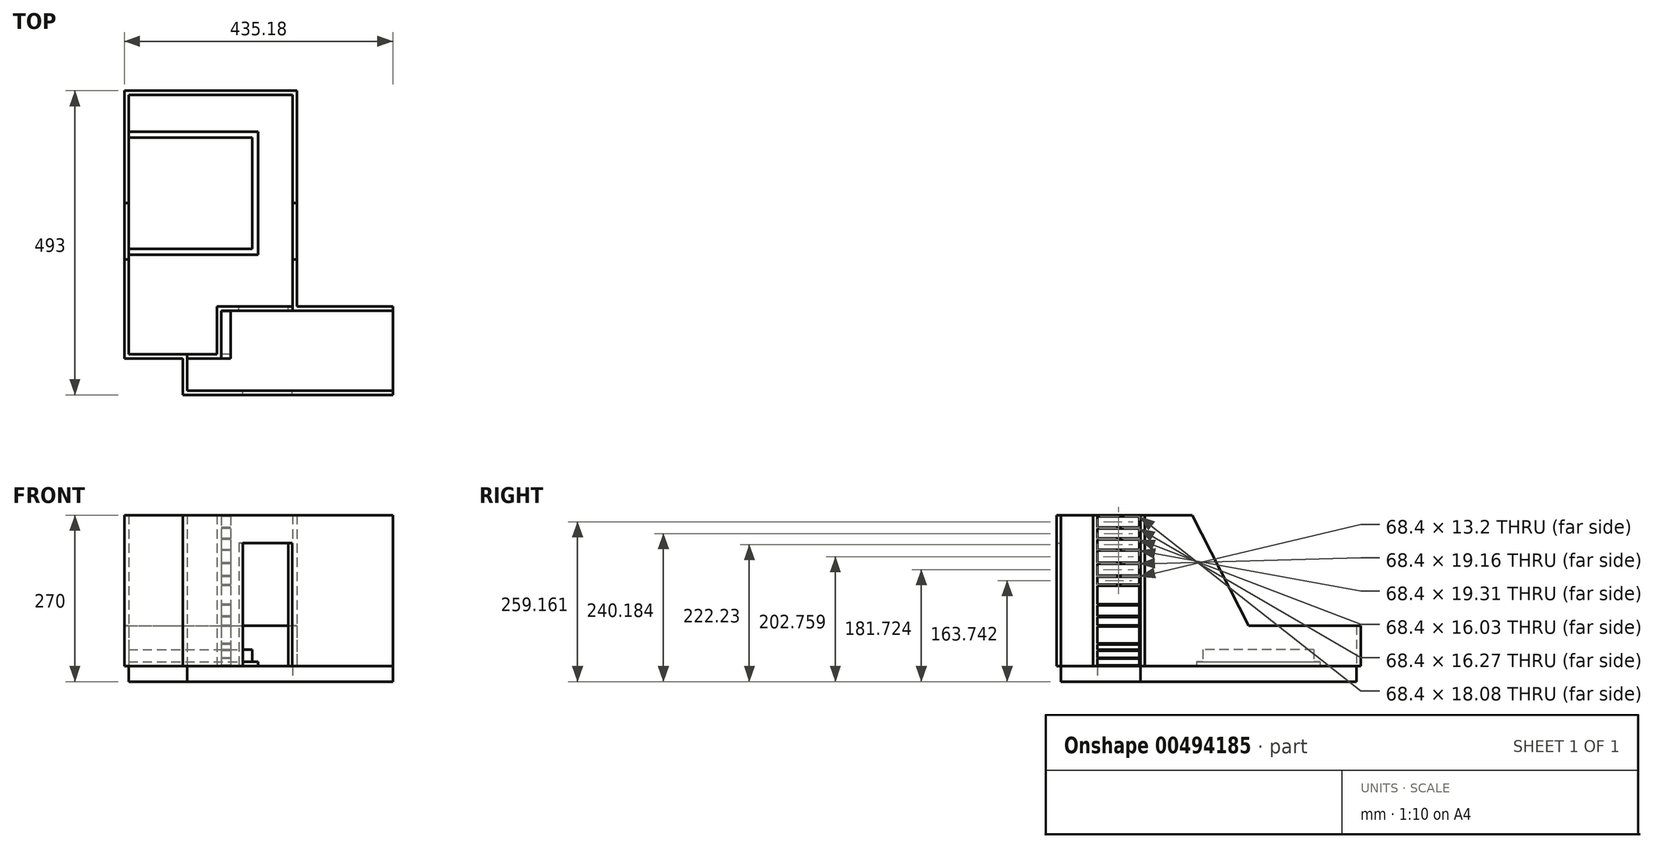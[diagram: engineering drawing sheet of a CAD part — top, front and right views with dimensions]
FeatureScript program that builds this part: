
annotation { "Feature Type Name" : "Feature", "Feature Type Description" : "" }
export const myFeature = defineFeature(function(context is Context, id is Id, definition is map)
    precondition{}
    {
        {
            var Q0;
            Q0=qCreatedBy(makeId("Top.planeOp"),FACE);
            var sketch = newSketch(context, id + "F0", { "sketchPlane" : qUnion([Q0])});
            skLineSegment(sketch, "E0.bottom", {"start": v(133, 175) * mm, "end": v(-133, 175) * mm});
            skLineSegment(sketch, "E0.top", {"start": v(133, -175) * mm, "end": v(-133, -175) * mm});
            skLineSegment(sketch, "E0.left", {"start": v(133, 175) * mm, "end": v(133, -175) * mm});
            skLineSegment(sketch, "E0.right", {"start": v(-133, 175) * mm, "end": v(-133, -175) * mm});
            skPoint(sketch, "E0.middle", {"position": v(0, 0) * mm});
            skLineSegment(sketch, "E1.bottom", {"start": v(-133, -175) * mm, "end": v(-38, -175) * mm});
            skLineSegment(sketch, "E1.top", {"start": v(-133, -245) * mm, "end": v(-38, -245) * mm});
            skLineSegment(sketch, "E1.left", {"start": v(-133, -175) * mm, "end": v(-133, -245) * mm});
            skLineSegment(sketch, "E1.right", {"start": v(-38, -175) * mm, "end": v(-38, -245) * mm});
            skLineSegment(sketch, "E2.bottom", {"start": v(-38, -245) * mm, "end": v(13, -245) * mm});
            skLineSegment(sketch, "E2.top", {"start": v(-38, -175) * mm, "end": v(13, -175) * mm});
            skLineSegment(sketch, "E2.left", {"start": v(-38, -245) * mm, "end": v(-38, -175) * mm});
            skLineSegment(sketch, "E2.right", {"start": v(13, -245) * mm, "end": v(13, -175) * mm});
            skLineSegment(sketch, "E3.bottom", {"start": v(13, -245) * mm, "end": v(-38, -245) * mm});
            skLineSegment(sketch, "E3.top", {"start": v(13, -304) * mm, "end": v(-38, -304) * mm});
            skLineSegment(sketch, "E3.left", {"start": v(13, -245) * mm, "end": v(13, -304) * mm});
            skLineSegment(sketch, "E3.right", {"start": v(-38, -245) * mm, "end": v(-38, -304) * mm});
            skLineSegment(sketch, "E4.bottom", {"start": v(13, -175) * mm, "end": v(295.18, -175) * mm});
            skLineSegment(sketch, "E4.top", {"start": v(13, -304) * mm, "end": v(295.18, -304) * mm});
            skLineSegment(sketch, "E4.left", {"start": v(13, -175) * mm, "end": v(13, -304) * mm});
            skLineSegment(sketch, "E4.right", {"start": v(295.18, -175) * mm, "end": v(295.18, -304) * mm});
            skLineSegment(sketch, "E5", {"start": v(45, -175) * mm, "end": v(45, -134.93) * mm});
            skSolve(sketch);
        }
        {
            var Q0;
            Q0 = qSketchRegion(id + "F0", true);
            extrude(context, id + "F1", {"entities" : qUnion([Q0]), "depth" : 25 * mm});
        }
        {
            var Q0;
            Q0=makeQuery(id+"F1.opExtrude","CAP_FACE",FACE,{"disambiguationData":[OSD([sQuery(id+"F0.wireOp",EDGE,"E0.bottom"),sQuery(id+"F0.wireOp",EDGE,"E0.top"),sQuery(id+"F0.wireOp",EDGE,"E0.left"),sQuery(id+"F0.wireOp",EDGE,"E0.right"),sQuery(id+"F0.wireOp",EDGE,"E1.top"),sQuery(id+"F0.wireOp",EDGE,"E1.left"),sQuery(id+"F0.wireOp",EDGE,"E2.right"),sQuery(id+"F0.wireOp",EDGE,"E3.top"),sQuery(id+"F0.wireOp",EDGE,"E3.left"),sQuery(id+"F0.wireOp",EDGE,"E3.right")])],"isStart":false});
            var sketch = newSketch(context, id + "F2", { "sketchPlane" : qUnion([Q0])});
            skLineSegment(sketch, "E6", {"start": v(-53.94, -329.4) * mm, "end": v(-53.94, -329.4) * mm});
            skLineSegment(sketch, "E7.0", {"start": v(295.18, -311) * mm, "end": v(-45, -311) * mm});
            skLineSegment(sketch, "E7.1", {"start": v(-45, -252) * mm, "end": v(-45, -311) * mm});
            skLineSegment(sketch, "E7.2", {"start": v(-140, -252) * mm, "end": v(-45, -252) * mm});
            skLineSegment(sketch, "E7.3", {"start": v(140, -168) * mm, "end": v(295.18, -168) * mm});
            skLineSegment(sketch, "E7.4", {"start": v(140, 182) * mm, "end": v(140, -168) * mm});
            skLineSegment(sketch, "E7.5", {"start": v(140, 182) * mm, "end": v(-140, 182) * mm});
            skLineSegment(sketch, "E7.6", {"start": v(-140, 182) * mm, "end": v(-140, -252) * mm});
            skLineSegment(sketch, "E8.0", {"start": v(-38, -245) * mm, "end": v(-38, -304) * mm});
            skLineSegment(sketch, "E8.1", {"start": v(133, 175) * mm, "end": v(-133, 175) * mm});
            skLineSegment(sketch, "E8.2", {"start": v(-133, 175) * mm, "end": v(-133, -245) * mm});
            skLineSegment(sketch, "E8.3", {"start": v(295.18, -304) * mm, "end": v(-38, -304) * mm});
            skLineSegment(sketch, "E8.4", {"start": v(133, 175) * mm, "end": v(133, -175) * mm});
            skLineSegment(sketch, "E8.5", {"start": v(133, -175) * mm, "end": v(295.18, -175) * mm});
            skLineSegment(sketch, "E8.6", {"start": v(-133, -245) * mm, "end": v(-38, -245) * mm});
            skLineSegment(sketch, "E9", {"start": v(295.18, -175) * mm, "end": v(295.18, -168) * mm});
            skLineSegment(sketch, "E10", {"start": v(295.18, -304) * mm, "end": v(295.18, -311) * mm});
            skSolve(sketch);
        }
        {
            var Q0;
            Q0=makeQuery(id+"F2.imprint","IMPRINT",FACE,{"disambiguationData":[TD([[makeQuery(id+"F2.imprint","IMPRINT",EDGE,{"derivedFrom":sQuery(id+"F2.wireOp",EDGE,"E7.0")}),-1.0]])]});
            extrude(context, id + "F3", {"entities" : qUnion([Q0]), "depth" : 245 * mm});
        }
        {
            var Q0;
            Q0=makeQuery(id+"F1.opExtrude","CAP_FACE",FACE,{"disambiguationData":[OSD([sQuery(id+"F0.wireOp",EDGE,"E0.bottom"),sQuery(id+"F0.wireOp",EDGE,"E0.left"),sQuery(id+"F0.wireOp",EDGE,"E0.right"),sQuery(id+"F0.wireOp",EDGE,"E1.top"),sQuery(id+"F0.wireOp",EDGE,"E1.left"),sQuery(id+"F0.wireOp",EDGE,"E3.top"),sQuery(id+"F0.wireOp",EDGE,"E3.right"),sQuery(id+"F0.wireOp",EDGE,"E4.bottom"),sQuery(id+"F0.wireOp",EDGE,"E4.top"),sQuery(id+"F0.wireOp",EDGE,"E4.right")])],"isStart":false});
            var sketch = newSketch(context, id + "F4", { "sketchPlane" : qUnion([Q0])});
            skLineSegment(sketch, "E11", {"start": v(133, -175) * mm, "end": v(17.35, -175) * mm});
            skLineSegment(sketch, "E12", {"start": v(17.35, -175) * mm, "end": v(17.35, -252) * mm});
            skLineSegment(sketch, "E13", {"start": v(17.35, -252) * mm, "end": v(-38, -252) * mm});
            skLineSegment(sketch, "E14.0", {"start": v(10.35, -245) * mm, "end": v(-38, -245) * mm});
            skLineSegment(sketch, "E14.1", {"start": v(10.35, -168) * mm, "end": v(10.35, -245) * mm});
            skLineSegment(sketch, "E14.2", {"start": v(133, -168) * mm, "end": v(10.35, -168) * mm});
            skLineSegment(sketch, "E15", {"start": v(-38, -252) * mm, "end": v(-38, -245) * mm});
            skLineSegment(sketch, "E16", {"start": v(133, -175) * mm, "end": v(133, -168) * mm});
            skSolve(sketch);
        }
        {
            var Q0;
            Q0=makeQuery(id+"F4.imprint","IMPRINT",FACE,{"disambiguationData":[TD([[makeQuery(id+"F4.imprint","IMPRINT",EDGE,{"derivedFrom":sQuery(id+"F4.wireOp",EDGE,"E11")}),-1.0]])]});
            var Q1;
            Q1=makeQuery(id+"F3.opExtrude","CAP_FACE",FACE,{"disambiguationData":[OSD([sQuery(id+"F2.wireOp",EDGE,"E7.0"),sQuery(id+"F2.wireOp",EDGE,"E7.1"),sQuery(id+"F2.wireOp",EDGE,"E7.2"),sQuery(id+"F2.wireOp",EDGE,"E7.3"),sQuery(id+"F2.wireOp",EDGE,"E7.4"),sQuery(id+"F2.wireOp",EDGE,"E7.5"),sQuery(id+"F2.wireOp",EDGE,"E7.6"),sQuery(id+"F2.wireOp",EDGE,"E8.0"),sQuery(id+"F2.wireOp",EDGE,"E8.1"),sQuery(id+"F2.wireOp",EDGE,"E8.2"),sQuery(id+"F2.wireOp",EDGE,"E8.3"),sQuery(id+"F2.wireOp",EDGE,"E8.4"),sQuery(id+"F2.wireOp",EDGE,"E8.5"),sQuery(id+"F2.wireOp",EDGE,"E8.6"),sQuery(id+"F2.wireOp",EDGE,"E9"),sQuery(id+"F2.wireOp",EDGE,"E10")])],"isStart":false});
            extrude(context, id + "F5", {"entities" : qUnion([Q0]), "endBound" : BoundingType.UP_TO_SURFACE, "endBoundEntityFace" : qUnion([Q1]), "depth" : 245 * mm});
        }
        {
            var Q0;
            Q0=makeQuery(id+"F5.opExtrude","SWEPT_FACE",FACE,{"disambiguationData":[OSD([sQuery(id+"F4.wireOp",EDGE,"E14.2")])]});
            var sketch = newSketch(context, id + "F6", { "sketchPlane" : qUnion([Q0])});
            skLineSegment(sketch, "E17.bottom", {"start": v(-126, 25) * mm, "end": v(-46, 25) * mm});
            skLineSegment(sketch, "E17.top", {"start": v(-126, 225) * mm, "end": v(-46, 225) * mm});
            skLineSegment(sketch, "E17.left", {"start": v(-126, 25) * mm, "end": v(-126, 225) * mm});
            skLineSegment(sketch, "E17.right", {"start": v(-46, 25) * mm, "end": v(-46, 225) * mm});
            skSolve(sketch);
        }
        {
            var Q0;
            Q0=makeQuery(id+"F6.imprint","IMPRINT",FACE,{"disambiguationData":[TD([[makeQuery(id+"F6.imprint","IMPRINT",EDGE,{"derivedFrom":sQuery(id+"F6.wireOp",EDGE,"E17.bottom")}),1.0]])]});
            extrude(context, id + "F7", {"entities" : qUnion([Q0]), "operationType" : NewBodyOperationType.REMOVE, "oppositeDirection" : true, "depth" : 25 * mm});
        }
        {
            var Q0;
            Q0=makeQuery(id+"F1.opExtrude","CAP_FACE",FACE,{"disambiguationData":[OSD([sQuery(id+"F0.wireOp",EDGE,"E0.bottom"),sQuery(id+"F0.wireOp",EDGE,"E0.top"),sQuery(id+"F0.wireOp",EDGE,"E0.left"),sQuery(id+"F0.wireOp",EDGE,"E0.right"),sQuery(id+"F0.wireOp",EDGE,"E1.top"),sQuery(id+"F0.wireOp",EDGE,"E1.left"),sQuery(id+"F0.wireOp",EDGE,"E2.right"),sQuery(id+"F0.wireOp",EDGE,"E3.top"),sQuery(id+"F0.wireOp",EDGE,"E3.left"),sQuery(id+"F0.wireOp",EDGE,"E3.right")])],"isStart":false});
            var sketch = newSketch(context, id + "F8", { "sketchPlane" : qUnion([Q0])});
            skLineSegment(sketch, "E18.bottom", {"start": v(-133, -84.24) * mm, "end": v(77, -84.24) * mm});
            skLineSegment(sketch, "E18.top", {"start": v(-133, 115.76) * mm, "end": v(77, 115.76) * mm});
            skLineSegment(sketch, "E18.left", {"start": v(-133, -84.24) * mm, "end": v(-133, 115.76) * mm});
            skLineSegment(sketch, "E18.right", {"start": v(77, -84.24) * mm, "end": v(77, 115.76) * mm});
            skSolve(sketch);
        }
        {
            var Q0;
            Q0 = qSketchRegion(id + "F8", true);
            extrude(context, id + "F9", {"entities" : qUnion([Q0]), "depth" : 7 * mm});
        }
        {
            var Q0;
            Q0=makeQuery(id+"F9.opExtrude","CAP_FACE",FACE,{"disambiguationData":[OSD([sQuery(id+"F8.wireOp",EDGE,"E18.bottom"),sQuery(id+"F8.wireOp",EDGE,"E18.top"),sQuery(id+"F8.wireOp",EDGE,"E18.left"),sQuery(id+"F8.wireOp",EDGE,"E18.right")])],"isStart":false});
            var sketch = newSketch(context, id + "F10", { "sketchPlane" : qUnion([Q0])});
            skLineSegment(sketch, "E19.bottom", {"start": v(-133, -74.24) * mm, "end": v(67, -74.24) * mm});
            skLineSegment(sketch, "E19.top", {"start": v(-133, 105.76) * mm, "end": v(67, 105.76) * mm});
            skLineSegment(sketch, "E19.left", {"start": v(-133, -74.24) * mm, "end": v(-133, 105.76) * mm});
            skLineSegment(sketch, "E19.right", {"start": v(67, -74.24) * mm, "end": v(67, 105.76) * mm});
            skSolve(sketch);
        }
        {
            var Q0;
            Q0=makeQuery(id+"F10.imprint","IMPRINT",FACE,{"disambiguationData":[TD([[makeQuery(id+"F10.imprint","IMPRINT",EDGE,{"derivedFrom":sQuery(id+"F10.wireOp",EDGE,"E19.bottom")}),1.0]])]});
            extrude(context, id + "F11", {"entities" : qUnion([Q0]), "operationType" : NewBodyOperationType.ADD, "depth" : 20 * mm});
        }
        {
            var Q0;
            Q0=makeQuery(id+"F3.opExtrude","SWEPT_FACE",FACE,{"disambiguationData":[OSD([sQuery(id+"F2.wireOp",EDGE,"E7.6")])]});
            var sketch = newSketch(context, id + "F12", { "sketchPlane" : qUnion([Q0])});
            skLineSegment(sketch, "E20", {"start": v(-215.94, 90.95) * mm, "end": v(0, 90.95) * mm});
            skLineSegment(sketch, "E21", {"start": v(0, 90.95) * mm, "end": v(91.43, 270) * mm});
            skLineSegment(sketch, "E22", {"start": v(91.43, 270) * mm, "end": v(91.43, 327.14) * mm});
            skLineSegment(sketch, "E23", {"start": v(91.43, 327.14) * mm, "end": v(-215.94, 327.14) * mm});
            skLineSegment(sketch, "E24", {"start": v(-215.94, 327.14) * mm, "end": v(-215.94, 61.64) * mm});
            skLineSegment(sketch, "E25", {"start": v(-215.94, 61.64) * mm, "end": v(-215.94, 90.95) * mm});
            skSolve(sketch);
        }
        {
            var Q0;
            Q0 = qSketchRegion(id + "F12", true);
            extrude(context, id + "F13", {"entities" : qUnion([Q0]), "operationType" : NewBodyOperationType.REMOVE, "endBound" : BoundingType.THROUGH_ALL, "oppositeDirection" : true, "depth" : 25 * mm});
        }
        {
            var Q0;
            Q0=makeQuery(id+"F3.opExtrude","SWEPT_FACE",FACE,{"disambiguationData":[OSD([sQuery(id+"F2.wireOp",EDGE,"E8.3")])]});
            var sketch = newSketch(context, id + "F14", { "sketchPlane" : qUnion([Q0])});
            skLineSegment(sketch, "E26.bottom", {"start": v(-132, 25) * mm, "end": v(-52, 25) * mm});
            skLineSegment(sketch, "E26.top", {"start": v(-132, 225) * mm, "end": v(-52, 225) * mm});
            skLineSegment(sketch, "E26.left", {"start": v(-132, 25) * mm, "end": v(-132, 225) * mm});
            skLineSegment(sketch, "E26.right", {"start": v(-52, 25) * mm, "end": v(-52, 225) * mm});
            skSolve(sketch);
        }
        {
            var Q0;
            Q0=makeQuery(id+"F14.imprint","IMPRINT",FACE,{"disambiguationData":[TD([[makeQuery(id+"F14.imprint","IMPRINT",EDGE,{"derivedFrom":sQuery(id+"F14.wireOp",EDGE,"E26.bottom")}),1.0]])]});
            extrude(context, id + "F15", {"entities" : qUnion([Q0]), "operationType" : NewBodyOperationType.REMOVE, "oppositeDirection" : true, "depth" : 25 * mm});
        }
        {
            var Q0;
            Q0=makeQuery(id+"F5.opExtrude","SWEPT_FACE",FACE,{"disambiguationData":[OSD([sQuery(id+"F4.wireOp",EDGE,"E12")])]});
            var sketch = newSketch(context, id + "F16", { "sketchPlane" : qUnion([Q0])});
            skLineSegment(sketch, "E27.bottom", {"start": v(-252, 25) * mm, "end": v(-175, 25) * mm});
            skLineSegment(sketch, "E27.top", {"start": v(-252, 270) * mm, "end": v(-175, 270) * mm});
            skLineSegment(sketch, "E27.left", {"start": v(-252, 25) * mm, "end": v(-252, 270) * mm});
            skLineSegment(sketch, "E27.right", {"start": v(-175, 25) * mm, "end": v(-175, 270) * mm});
            skLineSegment(sketch, "E28.1", {"start": v(-245.2, 26.8) * mm, "end": v(-176.8, 26.8) * mm});
            skLineSegment(sketch, "E28.3", {"start": v(-245.2, 268.2) * mm, "end": v(-176.8, 268.2) * mm});
            skLineSegment(sketch, "E29", {"start": v(-245.2, 248.32) * mm, "end": v(-176.8, 248.32) * mm});
            skLineSegment(sketch, "E30", {"start": v(-245.2, 230.25) * mm, "end": v(-176.8, 230.25) * mm});
            skLineSegment(sketch, "E31", {"start": v(-245.2, 212.41) * mm, "end": v(-176.8, 212.41) * mm});
            skLineSegment(sketch, "E32", {"start": v(-245.2, 191.3) * mm, "end": v(-176.8, 191.3) * mm});
            skLineSegment(sketch, "E33", {"start": v(-245.2, 170.34) * mm, "end": v(-176.8, 170.34) * mm});
            skLineSegment(sketch, "E34", {"start": v(-245.2, 155.34) * mm, "end": v(-176.8, 155.34) * mm});
            skLineSegment(sketch, "E35", {"start": v(-245.2, 125.36) * mm, "end": v(-176.8, 125.36) * mm});
            skLineSegment(sketch, "E36", {"start": v(-245.2, 106.3) * mm, "end": v(-176.8, 106.3) * mm});
            skLineSegment(sketch, "E37", {"start": v(-245.2, 91.46) * mm, "end": v(-176.8, 91.46) * mm});
            skLineSegment(sketch, "E38", {"start": v(-245.2, 62.15) * mm, "end": v(-176.8, 62.15) * mm});
            skLineSegment(sketch, "E39", {"start": v(-245.2, 60.35) * mm, "end": v(-176.8, 60.35) * mm});
            skLineSegment(sketch, "E40", {"start": v(-245.2, 38.88) * mm, "end": v(-176.8, 38.88) * mm});
            skLineSegment(sketch, "E41.bottom", {"start": v(-245.2, 50.24) * mm, "end": v(-176.8, 50.24) * mm});
            skLineSegment(sketch, "E41.top", {"start": v(-245.2, 52.04) * mm, "end": v(-176.8, 52.04) * mm});
            skLineSegment(sketch, "E42", {"start": v(-245.2, 89.66) * mm, "end": v(-176.8, 89.66) * mm});
            skLineSegment(sketch, "E43", {"start": v(-176.8, 104.5) * mm, "end": v(-245.2, 104.5) * mm});
            skLineSegment(sketch, "E44", {"start": v(-245.2, 123.56) * mm, "end": v(-176.8, 123.56) * mm});
            skLineSegment(sketch, "E45", {"start": v(-176.8, 157.14) * mm, "end": v(-245.2, 157.14) * mm});
            skLineSegment(sketch, "E46", {"start": v(-245.2, 172.14) * mm, "end": v(-176.8, 172.14) * mm});
            skLineSegment(sketch, "E47", {"start": v(-176.8, 193.1) * mm, "end": v(-245.2, 193.1) * mm});
            skLineSegment(sketch, "E48", {"start": v(-245.2, 214.21) * mm, "end": v(-176.8, 214.21) * mm});
            skLineSegment(sketch, "E49", {"start": v(-176.8, 250.12) * mm, "end": v(-245.2, 250.12) * mm});
            skLineSegment(sketch, "E50", {"start": v(-245.2, 232.05) * mm, "end": v(-176.8, 232.05) * mm});
            skLineSegment(sketch, "E51", {"start": v(-245.2, 37.08) * mm, "end": v(-176.8, 37.08) * mm});
            skLineSegment(sketch, "E52", {"start": v(-245.2, 268.2) * mm, "end": v(-245.2, 250.12) * mm});
            skLineSegment(sketch, "E53", {"start": v(-245.2, 248.32) * mm, "end": v(-245.2, 232.05) * mm});
            skLineSegment(sketch, "E54", {"start": v(-245.2, 230.25) * mm, "end": v(-245.2, 214.21) * mm});
            skLineSegment(sketch, "E55", {"start": v(-245.2, 212.41) * mm, "end": v(-245.2, 193.1) * mm});
            skLineSegment(sketch, "E56", {"start": v(-245.2, 191.3) * mm, "end": v(-245.2, 172.14) * mm});
            skLineSegment(sketch, "E57", {"start": v(-245.2, 170.34) * mm, "end": v(-245.2, 157.14) * mm});
            skLineSegment(sketch, "E58", {"start": v(-245.2, 155.34) * mm, "end": v(-245.2, 125.36) * mm});
            skLineSegment(sketch, "E59", {"start": v(-245.2, 123.56) * mm, "end": v(-245.2, 106.3) * mm});
            skLineSegment(sketch, "E60", {"start": v(-245.2, 104.5) * mm, "end": v(-245.2, 91.46) * mm});
            skLineSegment(sketch, "E61", {"start": v(-245.2, 89.66) * mm, "end": v(-245.2, 62.15) * mm});
            skLineSegment(sketch, "E62", {"start": v(-245.2, 60.35) * mm, "end": v(-245.2, 52.04) * mm});
            skLineSegment(sketch, "E63", {"start": v(-245.2, 50.24) * mm, "end": v(-245.2, 38.88) * mm});
            skLineSegment(sketch, "E64", {"start": v(-245.2, 37.08) * mm, "end": v(-245.2, 26.8) * mm});
            skLineSegment(sketch, "E65", {"start": v(-176.8, 60.35) * mm, "end": v(-176.8, 52.04) * mm});
            skLineSegment(sketch, "E66", {"start": v(-176.8, 37.08) * mm, "end": v(-176.8, 26.8) * mm});
            skLineSegment(sketch, "E67", {"start": v(-176.8, 38.88) * mm, "end": v(-176.8, 50.24) * mm});
            skLineSegment(sketch, "E68", {"start": v(-176.8, 62.15) * mm, "end": v(-176.8, 89.66) * mm});
            skLineSegment(sketch, "E69", {"start": v(-176.8, 91.46) * mm, "end": v(-176.8, 104.5) * mm});
            skLineSegment(sketch, "E70", {"start": v(-176.8, 106.3) * mm, "end": v(-176.8, 123.56) * mm});
            skLineSegment(sketch, "E71", {"start": v(-176.8, 125.36) * mm, "end": v(-176.8, 155.34) * mm});
            skLineSegment(sketch, "E72", {"start": v(-176.8, 157.14) * mm, "end": v(-176.8, 170.34) * mm});
            skLineSegment(sketch, "E73", {"start": v(-176.8, 172.14) * mm, "end": v(-176.8, 191.3) * mm});
            skLineSegment(sketch, "E74", {"start": v(-176.8, 193.1) * mm, "end": v(-176.8, 212.41) * mm});
            skLineSegment(sketch, "E75", {"start": v(-176.8, 214.21) * mm, "end": v(-176.8, 230.25) * mm});
            skLineSegment(sketch, "E76", {"start": v(-176.8, 232.05) * mm, "end": v(-176.8, 248.32) * mm});
            skLineSegment(sketch, "E77", {"start": v(-176.8, 250.12) * mm, "end": v(-176.8, 268.2) * mm});
            skSolve(sketch);
        }
        {
            var Q0;
            Q0=makeQuery(id+"F16.imprint","IMPRINT",FACE,{"disambiguationData":[TD([[makeQuery(id+"F16.imprint","IMPRINT",EDGE,{"derivedFrom":sQuery(id+"F16.wireOp",EDGE,"E27.bottom")}),-1.0]])]});
            extrude(context, id + "F17", {"entities" : qUnion([Q0]), "depth" : 15 * mm});
        }
    });
